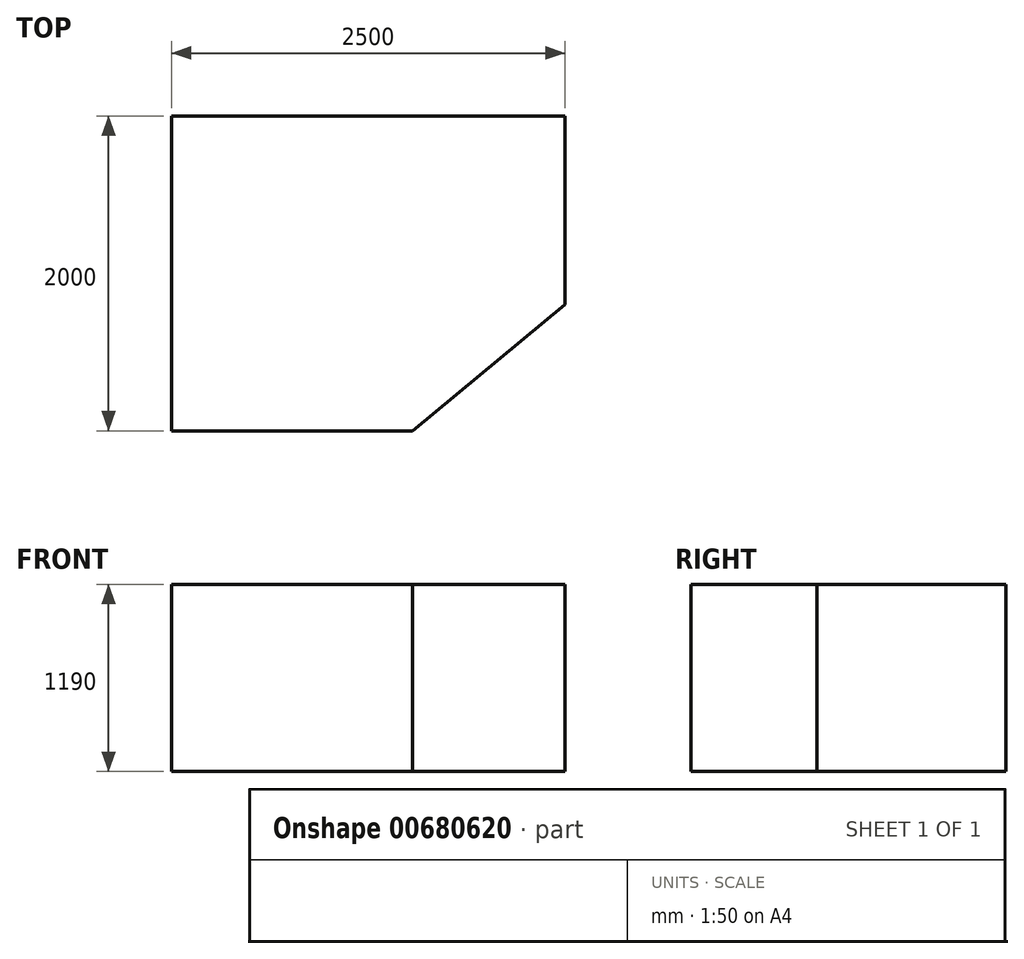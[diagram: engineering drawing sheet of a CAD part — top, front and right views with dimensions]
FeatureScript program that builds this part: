
annotation { "Feature Type Name" : "Feature", "Feature Type Description" : "" }
export const myFeature = defineFeature(function(context is Context, id is Id, definition is map)
    precondition{}
    {
        {
            var Q0;
            Q0=qCreatedBy(makeId("Top.planeOp"),FACE);
            var sketch = newSketch(context, id + "F0", { "sketchPlane" : qUnion([Q0])});
            skLineSegment(sketch, "E0.bottom", {"start": v(0, 0) * mm, "end": v(1530.88, 0) * mm});
            skLineSegment(sketch, "E0.top", {"start": v(0, 2000) * mm, "end": v(2500, 2000) * mm});
            skLineSegment(sketch, "E0.left", {"start": v(0, 0) * mm, "end": v(0, 2000) * mm});
            skLineSegment(sketch, "E0.right", {"start": v(2500, 800.59) * mm, "end": v(2500, 2000) * mm});
            skLineSegment(sketch, "E1", {"start": v(2500, 800.59) * mm, "end": v(1530.88, 0) * mm});
            skSolve(sketch);
        }
        {
            var Q0;
            Q0 = qSketchRegion(id + "F0", true);
            extrude(context, id + "F1", {"entities" : qUnion([Q0]), "depth" : 1190 * mm, "offsetDistance" : 25 * mm});
        }
    });
